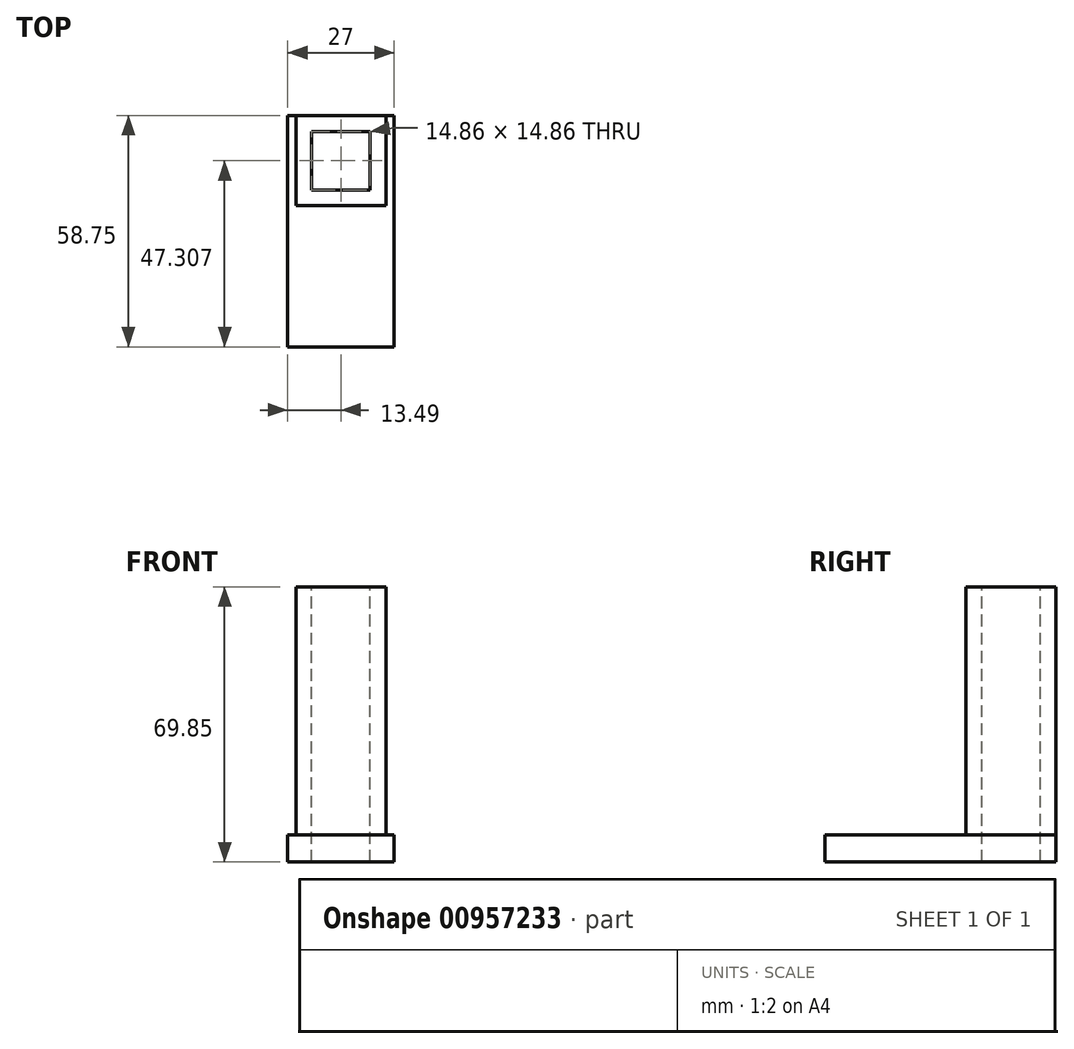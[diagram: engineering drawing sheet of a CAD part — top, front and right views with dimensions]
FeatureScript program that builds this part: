
annotation { "Feature Type Name" : "Feature", "Feature Type Description" : "" }
export const myFeature = defineFeature(function(context is Context, id is Id, definition is map)
    precondition{}
    {
        {
            var Q0;
            Q0=qCreatedBy(makeId("Top.planeOp"),FACE);
            var sketch = newSketch(context, id + "F0", { "sketchPlane" : qUnion([Q0])});
            skLineSegment(sketch, "E0.bottom", {"start": v(-35.02, -58.75) * mm, "end": v(-8.02, -58.75) * mm});
            skLineSegment(sketch, "E0.top", {"start": v(-35.02, 0) * mm, "end": v(-8.02, 0) * mm});
            skLineSegment(sketch, "E0.left", {"start": v(-35.02, -58.75) * mm, "end": v(-35.02, 0) * mm});
            skLineSegment(sketch, "E0.right", {"start": v(-8.02, -58.75) * mm, "end": v(-8.02, 0) * mm});
            skSolve(sketch);
        }
        {
            var Q0;
            Q0 = qSketchRegion(id + "F0", true);
            extrude(context, id + "F1", {"entities" : qUnion([Q0]), "depth" : 6.86 * mm, "offsetDistance" : 25.4 * mm});
        }
        {
            var Q0;
            Q0=qCreatedBy(makeId("Top.planeOp"),FACE);
            var sketch = newSketch(context, id + "F2", { "sketchPlane" : qUnion([Q0])});
            skLineSegment(sketch, "E1.bottom", {"start": v(-32.95, 0) * mm, "end": v(-10.09, 0) * mm});
            skLineSegment(sketch, "E1.top", {"start": v(-32.95, -22.86) * mm, "end": v(-10.09, -22.86) * mm});
            skLineSegment(sketch, "E1.left", {"start": v(-32.95, 0) * mm, "end": v(-32.95, -22.86) * mm});
            skLineSegment(sketch, "E1.right", {"start": v(-10.09, 0) * mm, "end": v(-10.09, -22.86) * mm});
            skLineSegment(sketch, "E2", {"start": v(-21.52, -22.86) * mm, "end": v(-21.52, 0) * mm});
            skSolve(sketch);
        }
        {
            var Q0;
            Q0 = qSketchRegion(id + "F2", true);
            extrude(context, id + "F3", {"entities" : qUnion([Q0]), "operationType" : NewBodyOperationType.ADD, "depth" : 69.85 * mm, "offsetDistance" : 25.4 * mm});
        }
        {
            var Q0;
            Q0=makeQuery(id+"F3.opExtrude","CAP_FACE",FACE,{"disambiguationData":[OSD([sQuery(id+"F2.wireOp",EDGE,"E1.bottom"),sQuery(id+"F2.wireOp",EDGE,"E1.top"),sQuery(id+"F2.wireOp",EDGE,"E1.left"),sQuery(id+"F2.wireOp",EDGE,"E1.right")])],"isStart":false});
            var sketch = newSketch(context, id + "F4", { "sketchPlane" : qUnion([Q0])});
            skLineSegment(sketch, "E3.bottom", {"start": v(-28.96, -18.87) * mm, "end": v(-14.1, -18.87) * mm});
            skLineSegment(sketch, "E3.top", {"start": v(-28.96, -4.01) * mm, "end": v(-14.1, -4.01) * mm});
            skLineSegment(sketch, "E3.left", {"start": v(-28.96, -18.87) * mm, "end": v(-28.96, -4.01) * mm});
            skLineSegment(sketch, "E3.right", {"start": v(-14.1, -18.87) * mm, "end": v(-14.1, -4.01) * mm});
            skSolve(sketch);
        }
        {
            var Q0;
            Q0=makeQuery(id+"F4.imprint","IMPRINT",FACE,{"disambiguationData":[TD([[makeQuery(id+"F4.imprint","IMPRINT",EDGE,{"derivedFrom":sQuery(id+"F4.wireOp",EDGE,"E3.bottom")}),1.0]])]});
            extrude(context, id + "F5", {"entities" : qUnion([Q0]), "operationType" : NewBodyOperationType.REMOVE, "oppositeDirection" : true, "depth" : 76.2 * mm, "offsetDistance" : 25.4 * mm});
        }
    });
